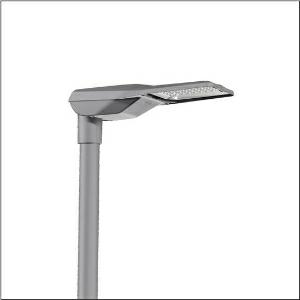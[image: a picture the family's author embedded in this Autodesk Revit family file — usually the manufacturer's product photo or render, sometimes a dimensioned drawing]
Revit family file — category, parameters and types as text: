
# Revit family: streetlight_sl_21_iq_mini___st1_0a_5xe2d41g08hb_63a2
name_source: partatom
category: Lighting Fixtures
units: mm (PartAtom-declared; Revit-internal decimal feet)

## family parameters
Cut with Voids When Loaded = No
Host = Face
Light Source = No
Part Type = Normal
Room Calculation Point = No
Round Connector Dimension = Use Diameter
Shared = No

## types (1)
- --- (1 x LED, 9860 lm, 70.9 W, 4000K)
    Apparent Load = 71 VA
    CIE Flux Codes = 37 72 97 100 100
    Color Rendering = 70
    Color Temperature = 4000K
    Default Elevation = 1800 mm
    Description = Streetlight SL 21 iQ mini, mast luminaire, primary light control with lens, of PMMA, primary optical cover: cover, of toughened safety glass, transparent, light distribution: ST1.0a, light emission: direct distribution, primary light characteristic: asymmetric, installation type: post-top, side-entry, LED, High Power LED, rated luminous flux: 9.860lm, luminous efficacy: 139lm/W, light colour: 740, colour temperature: 4000K, control gear: iQ Street-Remote, control: Street-Remote, Auto-Match, Temp-Guard, Lumen-Switch, Night-Set, Smart-Wire, Light-Fading, Desk-Remote (wireless, voltage-free reading and setting of iQ features in the workshop via application-optimized NFC function/RFID function), optimised constant luminous flux control (CLO 2.0), pre-setting: linear dimming characteristic, mains connection: 220..240V, AC, 50/60Hz, start of lifetime: 71W, end of service life: 75W, reduction: 31W, luminaire housing, of diecast aluminium, powder-coated, Siteco® metallic grey (DB 702S), corrosivity category C5 mid according to DIN EN ISO 12944, please order mast flange separately, inclination adjustable: 0°, 5°, 10°, 15°, sealing non-destructively replaceable, multi-level sealing system, length: 628mm, width: 235mm, height: 110mm, mast flange for spigot size: 42mm (side-entry): 5XC10008XM4, 60/48mm (side-entry/post-top): 5XC10108XM2, 76/60mm (side-entry/post-top): 5XC10108XM1, mounting height: 4..8m, protection rating (complete): IP66, insulation class (complete): insulation class II (safety insulation), certification: CE, ENEC, ENEC+, VDE, impact resistance: IK10, permissible operating ambient temperature for outdoor applications: -40..+50°C, standard-compliant lighting for roads and squares, packaging unit: 1 piece

Light Distribution: ST1.0a
    Height = 110 mm
    Lamp = 1 x LED
    Lamp Light Flux = 9860 lm
    Lamp Power = 70.9 W
    Lamp count = 1
    Length = 625 mm
    Luminous efficacy = 139 lm/W
    Manufacturer = Siteco
    ModVariant = No
    Model = 5XE2D41G08HB
    Number of Poles = 1
    OnlyDefault = Yes
    Power Factor = 1
    Product Name = Streetlight SL 21 iQ mini | ST1.0a
    Product group = mast luminaire | pylon top
    ProductGroupID = 6100
    Protection Class = Protection class II
    Protection Degree = IP 66
    RLX_Detail_Level = 1
    RLX_Emergency_Light_Flux = 0 lm
    RLX_Emergency_Type = 0
    RLX_Emergency_Type_DB = No
    RlxData = <blob elided: 26301 chars, md5=2671c7ee>
    Socket = socket
    Standby Power = 0 W
    System Light Flux = 9860 lm
    System Power = 71 W
    Type Comments = factory setting: luminous flux: 100 % | dim-lin: 254 | 711 mA
    Type Image = l_1003519.jpg
    URL = http://relux.com
    VarID = @adj_179515
    Voltage = 0 V
    Weight = 0.00 kg
    Width = 234 mm

## geometry (parser evidence)
native form markers: Blend x4, Sweep x11
no freeform markers — native parametric forms only
